# Revit family: Faucet-Lavatory-KOHLER-Purist-K-14404IN_1
name_source: partatom
category: Plumbing Fixtures
revit_build: Autodesk Revit 2017 (Build: 20160225_1515(x64)
units: mm (PartAtom-declared; Revit-internal decimal feet)

## family parameters
Cut with Voids When Loaded = No
Host = Face
OmniClass Number = 23.31.11.00
OmniClass Title = Faucets
Part Type = Normal
Room Calculation Point = No
Round Connector Dimension = Use Diameter
Shared = No

## types (4) — shared parameters
ADA Compliant = No
Assembly Code = D2010
CW Connection = Yes
Cold Water Inlet = Cold Water Inlet
Date Modified = 07/31/2020
Default Elevation = 36"
Drain Included = No
Flow Rate = 0 GPM
HW Connection = Yes
Handle Clearance = 3 1/4"
Height = 12"
Hot Water Inlet = Hot Water Inlet
Length = 6 1/4"
Manufacturer = KOHLER Co.
Master Format 2014 = 22 41 39
Master Format 2014 Name = Residential Faucets, Supplies, and Trim
Material = Solid Brass Construction
Pressure = 0.00 psi
Product Name = Purist
Spout Reach = 6 1/4"
URL = https://www.kohler.co.in
Vent Connection = No
Waste Connection = No
Waste Water Outlet = Waste Water Outlet
WaterSense Certified = No
Width = 2 1/4"

## per-type parameters (varying)
| type | Description | Finish | Model | Smile Handle | Straight Handle | Type |
| Straight Handle, CP-Polished Chrome | Single-handle bathroom sink faucet with straight lever handle | Kohler-Metal-CP-Polished_Chrome | K-14404IN-4AND-CP | No | Yes | 2 |
| Straight Handle, BL-Matte Black | Single-handle bathroom sink faucet with straight lever handle | Kohler-Metal-BL-Matte_Black | K-14404IN-4AND-BL | No | Yes | 3 |
| Straight Handle, BGD-Vibrant Moderne Brushed Gold | Single-handle bathroom sink faucet with straight lever handle | Kohler-Metal-BGD-Vibrant_Moderne_Brushed_Gold | K-14404IN-4AND-BGD | No | Yes | 4 |
| Smile Handle, CP-Polished Chrome | Single-hole bathroom sink faucet with smile design handle | Kohler-Metal-CP-Polished_Chrome | K-14404IN-4ND-CP | Yes | No | 1 |

## geometry (parser evidence)
native form markers: Sweep x4
no freeform markers — native parametric forms only
